# Revit family: Communication_Bosch_Speakers_MTS-6154-CARDIOID-43
name_source: partatom
category: Communication Devices
revit_build: Autodesk Revit 2018 (Build: 20180423_1000(x64)
units: mm (PartAtom-declared; Revit-internal decimal feet)

## family parameters
Always vertical = No
Cut with Voids When Loaded = No
Maintain Annotation Orientation = No
Part Type = Normal
Room Calculation Point = No
Round Connector Dimension = Use Diameter
Shared = Yes
Work Plane-Based = Yes

## types (4) — shared parameters
ArchitectsAndEngineersSpecs = https://products.electrovoice.com
Default Elevation = 1219 mm
Dimensions (H x W x D) = 1092 mm x 1092 mm x 1494 mm
Disclaimer = https://resources-boschsecurity-cdn.azureedge.net
Frequency range (-10 dB) = Full space with MTS full range preset (50 Hz - 20 kHz)
Horizontal Coverage = 40°
IFCExportAs = IfcAudioVisualAppliance
IP Rating = IP55
InstallationManual = https://products.electrovoice.com
Manufacturer = Electro Voice
Material = Multi-ply birch
Max. SPL = 155 dB
PlanningTools = https://products.electrovoice.com
Product Information = https://products.electrovoice.com
Product Website = https://products.electrovoice.com
URL = www.electrovoice.com
UniclassCode = Pr_70_75_36_50
UniclassTitle = Loudspeakers
Vertical Coverage = 30°

## per-type parameters (varying)
| type | FamType | MaterialRALColour | Product Description | Weight (Kg) | XMTI |
| MTS-6154-43CPWB Loudspeaker cardioid 40x30 PW blk | MTS-6154-CARDIOID-43 : MTS-6154-43CPWB Loudspeaker cardioid 40x30 PW blk | RAL 9005 black | Loudspeaker cardioid 40x30 PW blk | 198 | 3 |
| MTS-6154-43CPWW Loudspeaker cardioid 40x30 PW wht | MTS-6154-CARDIOID-43 : MTS-6154-43CPWW Loudspeaker cardioid 40x30 PW wht | RAL 9003 white | Loudspeaker cardioid 40x30 PW wht | 198 | 4 |
| MTS-6154-43CFWB Loudspeaker cardioid 40x30 FW blk | MTS-6154-CARDIOID-43 : MTS-6154-43CFWB Loudspeaker cardioid 40x30 FW blk | RAL 9005 black | Loudspeaker cardioid 40x30 FW blk | 213 | 1 |
| MTS-6154-43CFWW Loudspeaker cardioid 40x30 FW wht | MTS-6154-CARDIOID-43 : MTS-6154-43CFWW Loudspeaker cardioid 40x30 FW wht | RAL 9003 white | Loudspeaker cardioid 40x30 FW wht | 213 | 2 |

## geometry (parser evidence)
native form markers: Sweep x4
no freeform markers — native parametric forms only
